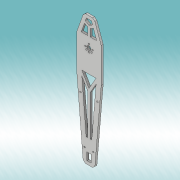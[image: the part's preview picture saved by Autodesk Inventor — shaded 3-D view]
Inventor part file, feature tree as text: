
AUTODESK INVENTOR PART (.ipt)
format: ipt  version: 2019 (Build 230136000, 136)  size: 216,064 bytes
history: native  units: mm
features: extrude x3, sketch x1
ambient origin geometry x8: Origin, YZ Plane, XZ Plane, XY Plane, X Axis, Y Axis, Z Axis, Center Point
bodies: Solid1 (feature_tree)
feature tree (4):
  extrude  "Extrusion1"  Depth=6.0mm
  extrude  "Extrusion2"  Depth=4.0mm
  extrude  "Extrusion3"  Depth=4.0mm
  sketch  "Sketch3"  dims[d0=7.0mm d1=6.0mm d2=145.0mm d3=68.0mm d4=37.0mm d5=48.0mm d8=24.43461mm d9=24.43461mm d10=15.0mm d11=6.0mm d12=4.0mm d13=3.0mm d14=5.0mm d15=25.0mm d17=100.0mm d19=5.0mm d20=28.0mm d21=150.0deg d29=6.0mm d32=6.0mm d33=4.0mm d38=3.0mm d40=4.0mm d41=0.0mm d42=2.9688mm d43=31.5mm d45=5.0mm d46=2.9688mm d47=17.0mm d48=6.0mm d51=200.0mm d54=3.0mm d56=14.0mm d57=8.0mm d58=7.0mm d59=50.0mm d61=180.0deg d63=5.0mm d64=5.0mm d65=17.453293mm d66=7.0mm d67=5.0mm d68=18.0mm d69=10.0mm d70=0.0mm d71=4.0mm d72=1.745329mm]
